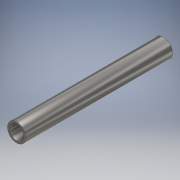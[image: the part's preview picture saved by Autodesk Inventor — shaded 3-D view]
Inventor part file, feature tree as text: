
AUTODESK INVENTOR PART (.ipt)
format: ipt  version: 2018 (Build 220112000, 112)  size: 101,888 bytes
history: native  units: mm
features: extrude x1, sketch x1
ambient origin geometry x8: Origin, YZ Plane, XZ Plane, XY Plane, X Axis, Y Axis, Z Axis, Center Point
bodies: Solid1 (feature_tree)
feature tree (2):
  extrude  "Extrusion1"  Depth=40.0mm
  sketch  "Sketch1"  dims[d0=4.0mm d1=5.0mm d2=40.0mm d3=0.0mm]
